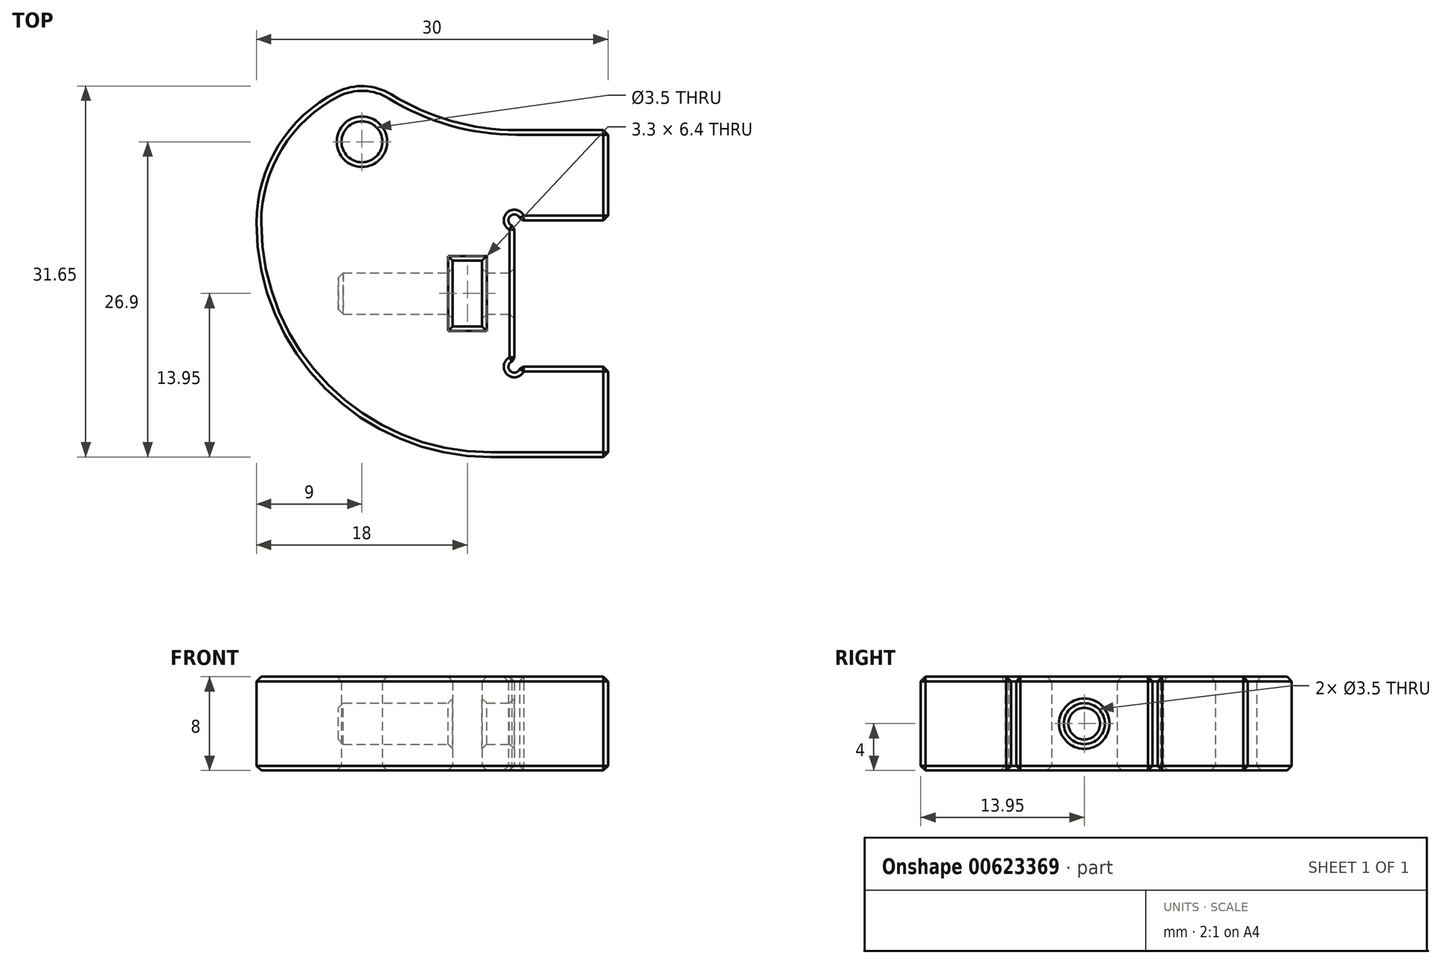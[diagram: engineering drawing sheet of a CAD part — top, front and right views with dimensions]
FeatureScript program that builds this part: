
annotation { "Feature Type Name" : "Feature", "Feature Type Description" : "" }
export const myFeature = defineFeature(function(context is Context, id is Id, definition is map)
    precondition{}
    {
        {
            var Q0;
            Q0=qCreatedBy(makeId("Top.planeOp"),FACE);
            var sketch = newSketch(context, id + "F0", { "sketchPlane" : qUnion([Q0])});
            skLineSegment(sketch, "E0", {"start": v(0, 0) * mm, "end": v(0, 7.7) * mm});
            skLineSegment(sketch, "E1", {"start": v(0, 0) * mm, "end": v(-8, 0) * mm});
            skLineSegment(sketch, "E2", {"start": v(-8, -12.5) * mm, "end": v(0, -12.5) * mm});
            skLineSegment(sketch, "E3", {"start": v(0, -12.5) * mm, "end": v(0, -20.2) * mm});
            skLineSegment(sketch, "E4", {"start": v(0, -20.2) * mm, "end": v(-10, -20.2) * mm});
            skLineSegment(sketch, "E5", {"start": v(-8, -6.25) * mm, "end": v(-45.43, -6.25) * mm, "construction": true});
            skLineSegment(sketch, "E6.bottom", {"start": v(-10.75, -3.45) * mm, "end": v(-13.25, -3.45) * mm});
            skLineSegment(sketch, "E6.top", {"start": v(-10.75, -9.05) * mm, "end": v(-13.25, -9.05) * mm});
            skLineSegment(sketch, "E6.left", {"start": v(-10.75, -3.45) * mm, "end": v(-10.75, -9.05) * mm});
            skLineSegment(sketch, "E6.right", {"start": v(-13.25, -3.45) * mm, "end": v(-13.25, -9.05) * mm});
            skPoint(sketch, "E6.middle", {"position": v(-12, -6.25) * mm});
            skCircle(sketch, "E7", {"center": v(-21, 6.7) * mm, "radius": 1.75 * mm});
            skPoint(sketch, "E8.visualSharp", {"position": v(-30, -20.2) * mm});
            skArc(sketch, "E8.filletArc", {"start": v(-30, -0.2) * mm, "mid": v(-24.14, -14.34) * mm, "end": v(-10, -20.2) * mm});
            skCircle(sketch, "E9", {"center": v(-8, 0) * mm, "radius": 0.5 * mm});
            skCircle(sketch, "E10", {"center": v(-8, -12.5) * mm, "radius": 0.5 * mm});
            skLineSegment(sketch, "E11", {"start": v(-8, 0) * mm, "end": v(-8, -12.5) * mm});
            skLineSegment(sketch, "E12", {"start": v(0, 7.7) * mm, "end": v(-30, 7.7) * mm});
            skLineSegment(sketch, "E13", {"start": v(-30, -0.2) * mm, "end": v(-30, 7.7) * mm});
            skCircle(sketch, "E14", {"center": v(-21, 6.7) * mm, "radius": 4.75 * mm});
            skSolve(sketch);
        }
        {
            var Q0;
            Q0=makeQuery(id+"F0.imprint","IMPRINT",FACE,{"disambiguationData":[TD([[makeQuery(id+"F0.imprint","IMPRINT",EDGE,{"derivedFrom":sQuery(id+"F0.wireOp",EDGE,"E0")}),1.0]])]});
            var Q1;
            {var subQ0=sQuery(id+"F0.wireOp",EDGE,"E12");var subQ1=sQuery(id+"F0.wireOp",EDGE,"E7");var subQ2=makeQuery(id+"F0.imprint","INTERSECT",VERTEX,{"disambiguationData":[OD(0.0)],"derivedFrom":[subQ1,subQ0]});Q1=makeQuery(id+"F0.imprint","IMPRINT",FACE,{"disambiguationData":[TD([[makeQuery(id+"F0.imprint","IMPRINT",EDGE,{"disambiguationData":[TD([[subQ2,1.0]])],"derivedFrom":subQ1}),-1.0]])]});}
            var Q2;
            {var subQ0=sQuery(id+"F0.wireOp",EDGE,"E12");var subQ1=sQuery(id+"F0.wireOp",EDGE,"E7");var subQ2=makeQuery(id+"F0.imprint","INTERSECT",VERTEX,{"disambiguationData":[OD(0.0)],"derivedFrom":[subQ1,subQ0]});Q2=makeQuery(id+"F0.imprint","IMPRINT",FACE,{"disambiguationData":[TD([[makeQuery(id+"F0.imprint","IMPRINT",EDGE,{"disambiguationData":[TD([[subQ2,-1.0]])],"derivedFrom":subQ1}),-1.0]])]});}
            extrude(context, id + "F1", {"entities" : qUnion([Q0, Q1, Q2]), "depth" : 8 * mm, "offsetDistance" : 25 * mm});
        }
        {
            var Q0;
            {var subQ0=sQuery(id+"F0.wireOp",EDGE,"E14");var subQ1=sQuery(id+"F0.wireOp",EDGE,"E12");Q0=makeQuery(id+"F1.opExtrude","SWEPT_EDGE",EDGE,{"disambiguationData":[OSD([subQ1,subQ0]),TDD([makeQuery(id+"F0.imprint","INTERSECT",VERTEX,{"disambiguationData":[OD(0.0)],"derivedFrom":[subQ1,subQ0]})])]});}
            fillet(context, id + "F2", {"entities" : qUnion([Q0]), "radius" : 20.32 * mm, "tangentPropagation" : true, "allowEdgeOverflow" : false});
        }
        {
            var Q0;
            {var subQ0=sQuery(id+"F0.wireOp",EDGE,"E14");var subQ1=sQuery(id+"F0.wireOp",EDGE,"E12");Q0=makeQuery(id+"F1.opExtrude","SWEPT_EDGE",EDGE,{"disambiguationData":[OSD([subQ1,subQ0]),TDD([makeQuery(id+"F0.imprint","INTERSECT",VERTEX,{"disambiguationData":[OD(1.0)],"derivedFrom":[subQ1,subQ0]})])]});}
            fillet(context, id + "F3", {"entities" : qUnion([Q0]), "radius" : 150 * mm, "tangentPropagation" : true, "allowEdgeOverflow" : false});
        }
        {
            var Q0;
            {var subQ0=sQuery(id+"F0.wireOp",EDGE,"E14");var subQ1=sQuery(id+"F0.wireOp",EDGE,"E12");Q0=makeQuery(id+"F3.opFillet","BLEND_EDGE",EDGE,{"blendedFrom":[makeQuery(id+"F1.opExtrude","SWEPT_EDGE",EDGE,{"disambiguationData":[OSD([subQ1,subQ0]),TDD([makeQuery(id+"F0.imprint","INTERSECT",VERTEX,{"disambiguationData":[OD(1.0)],"derivedFrom":[subQ1,subQ0]})])]}),makeQuery(id+"F1.opExtrude","SWEPT_FACE",FACE,{"disambiguationData":[OSD([sQuery(id+"F0.wireOp",EDGE,"E13")])]})],"blendedInto":[makeQuery(id+"F1.opExtrude","SWEPT_FACE",FACE,{"disambiguationData":[OSD([sQuery(id+"F0.wireOp",EDGE,"E13")])]})]});}
            fillet(context, id + "F4", {"entities" : qUnion([Q0]), "radius" : 12.5 * mm, "tangentPropagation" : true, "allowEdgeOverflow" : false});
        }
        {
            var Q0;
            Q0=makeQuery(id+"F1.opExtrude","SWEPT_FACE",FACE,{"disambiguationData":[OSD([sQuery(id+"F0.wireOp",EDGE,"E11")])]});
            var sketch = newSketch(context, id + "F5", { "sketchPlane" : qUnion([Q0])});
            skCircle(sketch, "E15", {"center": v(-6.25, 4) * mm, "radius": 1.75 * mm});
            skSolve(sketch);
        }
        {
            var Q0;
            Q0=makeQuery(id+"F5.imprint","IMPRINT",FACE,{"disambiguationData":[TD([[makeQuery(id+"F5.imprint","IMPRINT",EDGE,{"derivedFrom":sQuery(id+"F5.wireOp",EDGE,"E15")}),1.0]])]});
            extrude(context, id + "F6", {"entities" : qUnion([Q0]), "operationType" : NewBodyOperationType.REMOVE, "oppositeDirection" : true, "depth" : 15 * mm, "offsetDistance" : 25 * mm});
        }
        {
            var Q0;
            Q0=makeQuery(id+"F1.opExtrude","CAP_FACE",FACE,{"disambiguationData":[OSD([sQuery(id+"F0.wireOp",EDGE,"E0"),sQuery(id+"F0.wireOp",EDGE,"ENLcVbqI-dE6h-DvA8-kGz3-Un6j8AzGm7qQ"),sQuery(id+"F0.wireOp",EDGE,"E1"),sQuery(id+"F0.wireOp",EDGE,"th5AlzyC-4kuM-WVBd-E2pw-07Gsd2MfjMwf"),sQuery(id+"F0.wireOp",EDGE,"E2"),sQuery(id+"F0.wireOp",EDGE,"E3"),sQuery(id+"F0.wireOp",EDGE,"E4"),sQuery(id+"F0.wireOp",EDGE,"uwkoDh9o-9NeQ-P7v8-jeod-ReUs2frHVdsa.left"),sQuery(id+"F0.wireOp",EDGE,"c54f613d-0bb6-4fe1-9f87-684ae594c946"),sQuery(id+"F0.wireOp",EDGE,"E6.bottom"),sQuery(id+"F0.wireOp",EDGE,"E6.top"),sQuery(id+"F0.wireOp",EDGE,"E6.left"),sQuery(id+"F0.wireOp",EDGE,"E6.right"),sQuery(id+"F0.wireOp",EDGE,"E7"),sQuery(id+"F0.wireOp",EDGE,"QFiaZAi1-YPfK-LHQb-IRva-l0yyJdeQDXPB"),sQuery(id+"F0.wireOp",EDGE,"E8.filletArc"),sQuery(id+"F0.wireOp",EDGE,"ed6a5401-571d-4750-9c43-7ef2caef25f82")])],"isStart":false});
            var Q1;
            Q1=makeQuery(id+"F1.opExtrude","CAP_FACE",FACE,{"disambiguationData":[OSD([sQuery(id+"F0.wireOp",EDGE,"E0"),sQuery(id+"F0.wireOp",EDGE,"ENLcVbqI-dE6h-DvA8-kGz3-Un6j8AzGm7qQ"),sQuery(id+"F0.wireOp",EDGE,"E1"),sQuery(id+"F0.wireOp",EDGE,"th5AlzyC-4kuM-WVBd-E2pw-07Gsd2MfjMwf"),sQuery(id+"F0.wireOp",EDGE,"E2"),sQuery(id+"F0.wireOp",EDGE,"E3"),sQuery(id+"F0.wireOp",EDGE,"E4"),sQuery(id+"F0.wireOp",EDGE,"uwkoDh9o-9NeQ-P7v8-jeod-ReUs2frHVdsa.left"),sQuery(id+"F0.wireOp",EDGE,"c54f613d-0bb6-4fe1-9f87-684ae594c946"),sQuery(id+"F0.wireOp",EDGE,"E6.bottom"),sQuery(id+"F0.wireOp",EDGE,"E6.top"),sQuery(id+"F0.wireOp",EDGE,"E6.left"),sQuery(id+"F0.wireOp",EDGE,"E6.right"),sQuery(id+"F0.wireOp",EDGE,"E7"),sQuery(id+"F0.wireOp",EDGE,"QFiaZAi1-YPfK-LHQb-IRva-l0yyJdeQDXPB"),sQuery(id+"F0.wireOp",EDGE,"E8.filletArc"),sQuery(id+"F0.wireOp",EDGE,"ed6a5401-571d-4750-9c43-7ef2caef25f82")])],"isStart":true});
            var Q2;
            Q2=makeQuery(id+"F1.opExtrude","SWEPT_FACE",FACE,{"disambiguationData":[OSD([sQuery(id+"F0.wireOp",EDGE,"E3")])]});
            var Q3;
            Q3=makeQuery(id+"F1.opExtrude","SWEPT_FACE",FACE,{"disambiguationData":[OSD([sQuery(id+"F0.wireOp",EDGE,"E0")])]});
            var Q4;
            Q4=makeQuery(id+"F6.boolean.opBoolean","COPY",FACE,{"disambiguationData":[TD([makeQuery(id+"F1.opExtrude","SWEPT_FACE",FACE,{"disambiguationData":[OSD([sQuery(id+"F0.wireOp",EDGE,"E6.left")])]})])],"derivedFrom":makeQuery(id+"F6.opExtrude","SWEPT_FACE",FACE,{"disambiguationData":[OSD([sQuery(id+"F5.wireOp",EDGE,"E15")])]})});
            var Q5;
            {var subQ0=sQuery(id+"F5.wireOp",EDGE,"E15");Q5=makeQuery(id+"F6.boolean.opBoolean","COPY",FACE,{"disambiguationData":[TD([makeQuery(id+"F1.opExtrude","SWEPT_FACE",FACE,{"disambiguationData":[OSD([sQuery(id+"F0.wireOp",EDGE,"E6.right")])]})])],"derivedFrom":makeQuery(id+"F6.opExtrude","SWEPT_FACE",FACE,{"disambiguationData":[OSD([subQ0])]})});}
            var Q6;
            Q6=makeQuery(id+"F1.opExtrude","SWEPT_FACE",FACE,{"disambiguationData":[OSD([sQuery(id+"F0.wireOp",EDGE,"th5AlzyC-4kuM-WVBd-E2pw-07Gsd2MfjMwf"),sQuery(id+"F0.wireOp",EDGE,"uwkoDh9o-9NeQ-P7v8-jeod-ReUs2frHVdsa.left"),sQuery(id+"F0.wireOp",EDGE,"c54f613d-0bb6-4fe1-9f87-684ae594c946")])]});
            var Q7;
            Q7=makeQuery(id+"F1.opExtrude","SWEPT_FACE",FACE,{"disambiguationData":[OSD([sQuery(id+"F0.wireOp",EDGE,"E1")])]});
            var Q8;
            Q8=makeQuery(id+"F1.opExtrude","SWEPT_FACE",FACE,{"disambiguationData":[OSD([sQuery(id+"F0.wireOp",EDGE,"E2")])]});
            var Q9;
            Q9=makeQuery(id+"F1.opExtrude","SWEPT_FACE",FACE,{"disambiguationData":[OSD([sQuery(id+"F0.wireOp",EDGE,"E11")])]});
            chamfer(context, id + "F7", {"entities" : qUnion([Q0, Q1, Q2, Q3, Q4, Q5, Q6, Q7, Q8, Q9]), "width" : 0.4 * mm, "tangentPropagation" : true});
        }
    });
